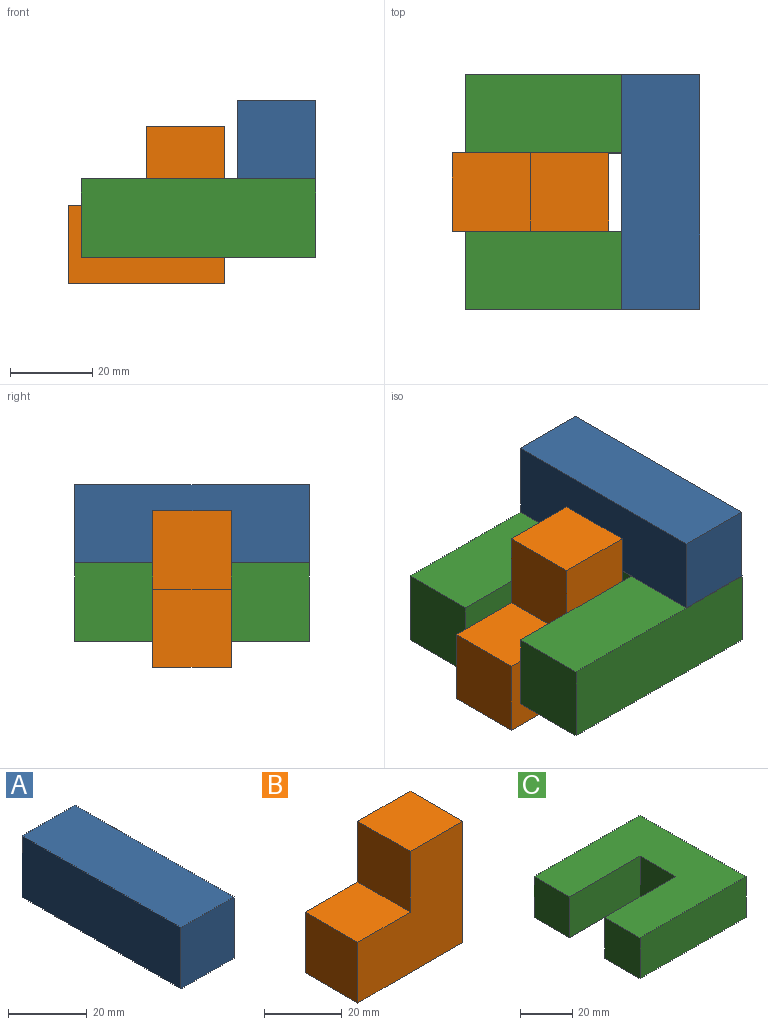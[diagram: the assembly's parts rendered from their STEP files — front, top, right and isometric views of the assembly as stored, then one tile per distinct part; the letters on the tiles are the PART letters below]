
ASSEMBLY  parts=3 mates=2
PART A: 6 faces, bbox 19.1x57.2x19.1 mm
  f0: plane 57.15x19.05mm, normal (0,0,1), area 1088.7mm2, adj f1,f3,f4,f5
  f1: plane 57.15x19.05mm, normal (-1,0,0), area 1088.7mm2, adj f0,f2,f4,f5
  f2: plane 57.15x19.05mm, normal (0,0,-1), area 1088.7mm2, adj f1,f3,f4,f5
  f3: plane 57.15x19.05mm, normal (1,0,0), area 1088.7mm2, adj f0,f2,f4,f5
  f4: plane 19.05x19.05mm, normal (0,-1,0), area 362.9mm2, adj f0,f1,f2,f3
  f5: plane 19.05x19.05mm, normal (0,1,0), area 362.9mm2, adj f0,f1,f2,f3
PART B: 8 faces, bbox 38.1x19.1x38.1 mm
  f0: plane 19.05x19.05mm, normal (0,0,1), area 362.9mm2, adj f1,f3,f4,f5
  f1: plane 19.05x19.05mm, normal (-1,0,0), area 362.9mm2, adj f0,f4,f5,f6
  f2: plane 38.1x19.05mm, normal (0,0,-1), area 725.8mm2, adj f3,f4,f5,f7
  f3: plane 38.1x19.05mm, normal (1,0,0), area 725.8mm2, adj f0,f2,f4,f5
  f4: plane 38.1x38.1mm, normal (0,-1,0), area 1088.7mm2, adj f0,f1,f2,f3,f6,f7
  f5: plane 38.1x38.1mm, normal (0,1,0), area 1088.7mm2, adj f0,f1,f2,f3,f6,f7
  f6: plane 19.05x19.05mm, normal (0,0,1), area 362.9mm2, adj f1,f4,f5,f7
  f7: plane 19.05x19.05mm, normal (-1,0,0), area 362.9mm2, adj f2,f4,f5,f6
PART C: 10 faces, bbox 57.2x57.2x19.1 mm
  f0: plane 19.05x19.05mm, normal (-1,0,0), area 362.9mm2, adj f1,f2,f6,f8
  f1: plane 57.15x57.15mm, normal (0,0,1), area 2540.3mm2, adj f0,f3,f4,f5,f6,f7,f8,f9
  f2: plane 57.15x57.15mm, normal (0,0,-1), area 2540.3mm2, adj f0,f3,f4,f5,f6,f7,f8,f9
  f3: plane 57.15x19.05mm, normal (1,0,0), area 1088.7mm2, adj f1,f2,f4,f5
  f4: plane 57.15x19.05mm, normal (0,-1,0), area 1088.7mm2, adj f1,f2,f3,f9
  f5: plane 57.15x19.05mm, normal (0,1,0), area 1088.7mm2, adj f1,f2,f3,f7
  f6: plane 38.1x19.05mm, normal (0,-1,0), area 725.8mm2, adj f0,f1,f2,f7
  f7: plane 19.05x19.05mm, normal (-1,0,0), area 362.9mm2, adj f1,f2,f5,f6
  f8: plane 38.1x19.05mm, normal (0,1,0), area 725.8mm2, adj f0,f1,f2,f9
  f9: plane 19.05x19.05mm, normal (-1,0,0), area 362.9mm2, adj f1,f2,f4,f8
PLACE A t=(15.73,25.8,-22.84)mm
PLACE B t=(-10.77,6.75,-24.11)mm
PLACE C t=(-25.8,25.8,-12.26)mm
MATE fastened C.f3 <-> A.f3  axis (1,0,0) through (-19.85,-31.35,21.9)mm
MATE fastened B.f5 <-> C.f6  axis (0,1,0) through (-57.95,6.75,12.38)mm
